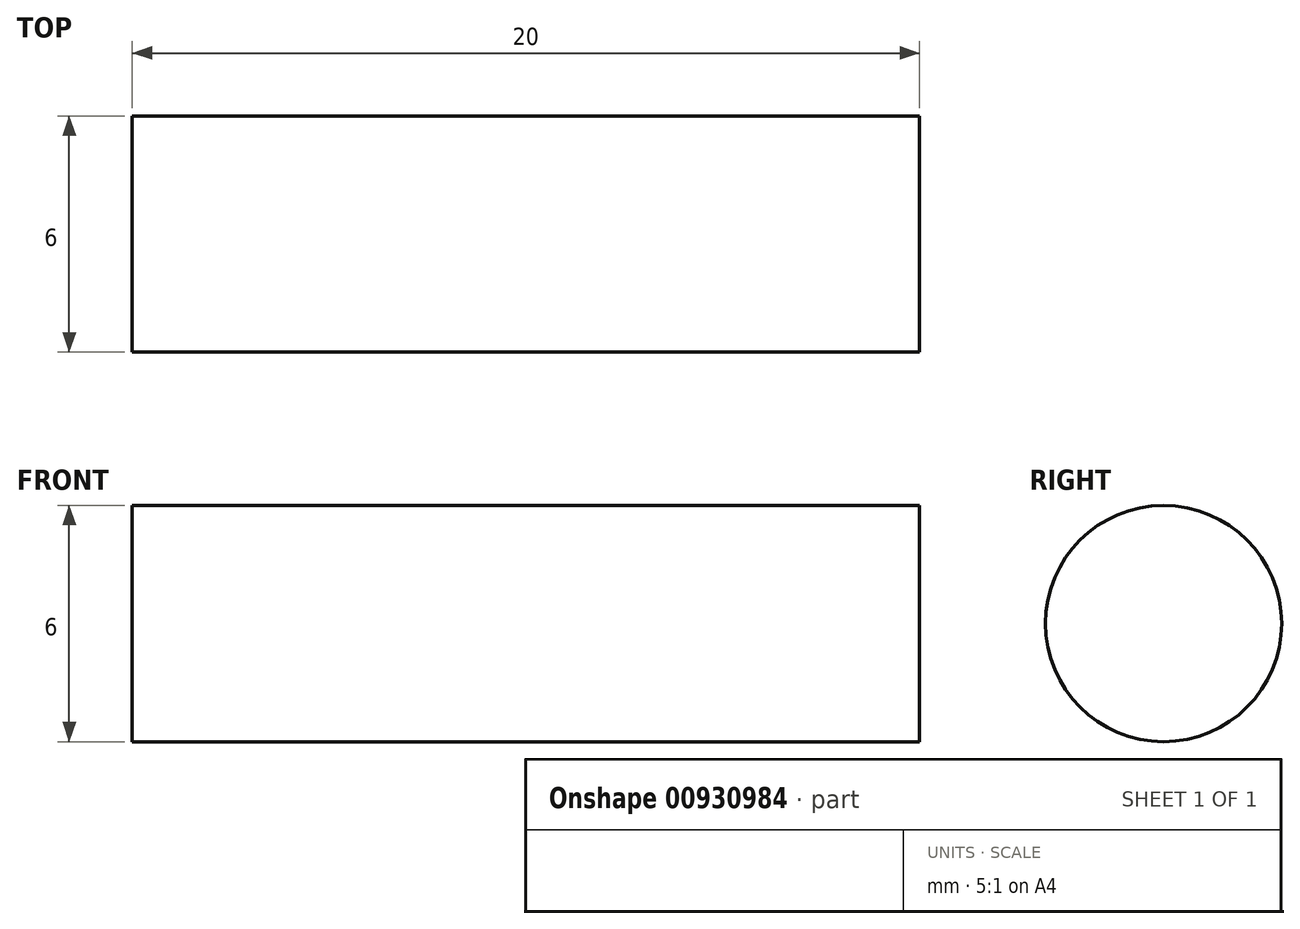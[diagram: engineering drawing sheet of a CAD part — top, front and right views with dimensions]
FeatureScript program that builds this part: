
annotation { "Feature Type Name" : "Feature", "Feature Type Description" : "" }
export const myFeature = defineFeature(function(context is Context, id is Id, definition is map)
    precondition{}
    {
        {
            var Q0;
            Q0=qCreatedBy(makeId("Right.planeOp"),FACE);
            var sketch = newSketch(context, id + "F0", { "sketchPlane" : qUnion([Q0])});
            skCircle(sketch, "E0", {"center": v(0, 0) * mm, "radius": 3 * mm});
            skSolve(sketch);
        }
        {
            var Q0;
            Q0 = qSketchRegion(id + "F0", true);
            extrude(context, id + "F1", {"entities" : qUnion([Q0]), "depth" : 20 * mm, "offsetDistance" : 25 * mm});
        }
    });
